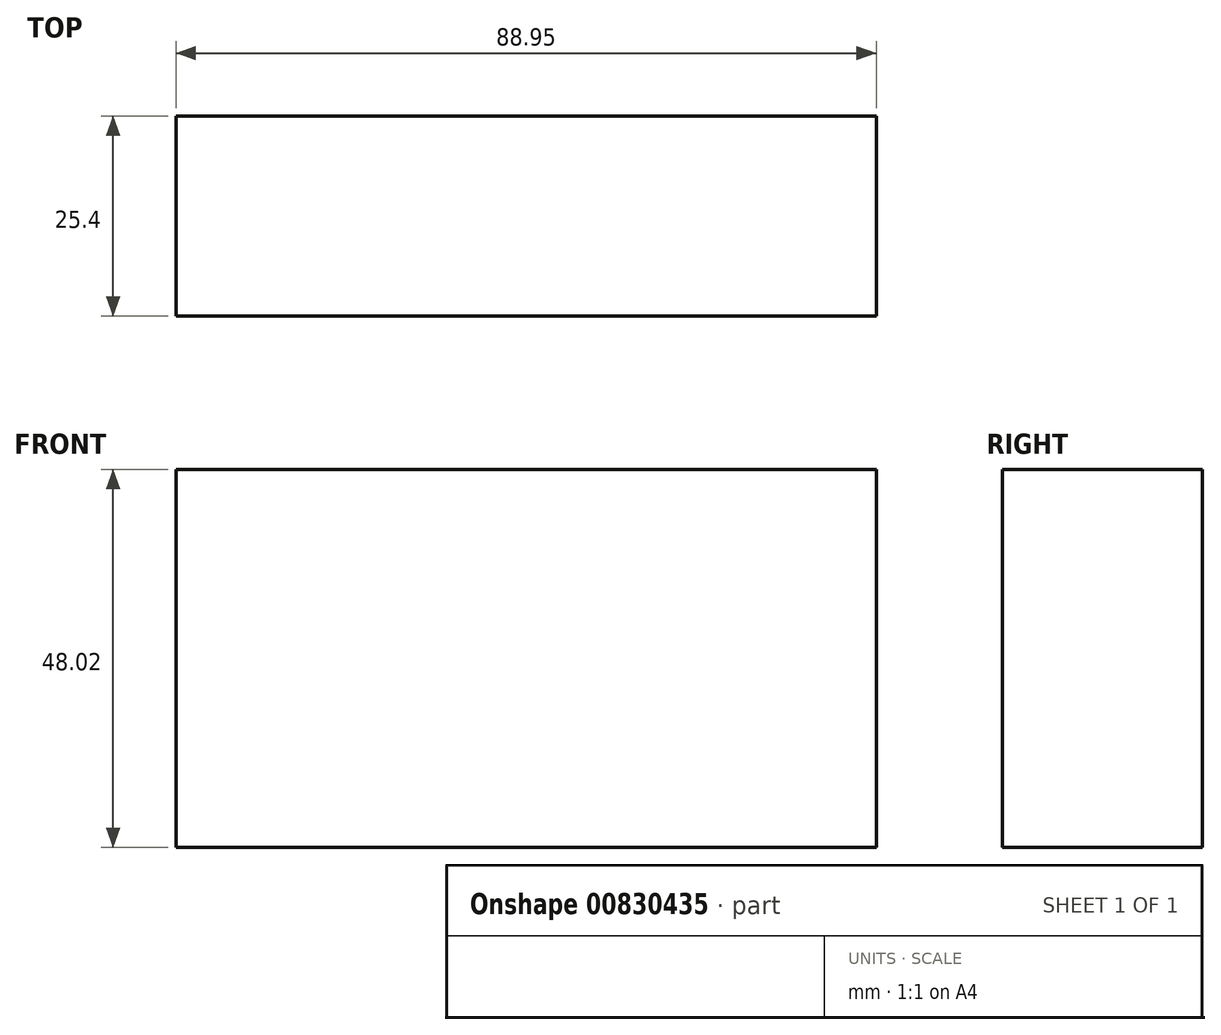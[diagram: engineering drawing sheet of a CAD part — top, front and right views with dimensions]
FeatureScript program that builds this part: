
annotation { "Feature Type Name" : "Feature", "Feature Type Description" : "" }
export const myFeature = defineFeature(function(context is Context, id is Id, definition is map)
    precondition{}
    {
        {
            var Q0;
            Q0=qCreatedBy(makeId("Front.planeOp"),FACE);
            var sketch = newSketch(context, id + "F0", { "sketchPlane" : qUnion([Q0])});
            skLineSegment(sketch, "E0.bottom", {"start": v(0, 0) * mm, "end": v(88.95, 0) * mm});
            skLineSegment(sketch, "E0.top", {"start": v(0, 48.02) * mm, "end": v(88.95, 48.02) * mm});
            skLineSegment(sketch, "E0.left", {"start": v(0, 0) * mm, "end": v(0, 48.02) * mm});
            skLineSegment(sketch, "E0.right", {"start": v(88.95, 0) * mm, "end": v(88.95, 48.02) * mm});
            skSolve(sketch);
        }
        {
            var Q0;
            Q0=makeQuery(id+"F0.imprint","IMPRINT",FACE,{"disambiguationData":[TD([[makeQuery(id+"F0.imprint","IMPRINT",EDGE,{"derivedFrom":sQuery(id+"F0.wireOp",EDGE,"E0.bottom")}),1.0]])]});
            extrude(context, id + "F1", {"entities" : qUnion([Q0]), "depth" : 25.4 * mm, "offsetDistance" : 25.4 * mm});
        }
    });
